# Revit family: Bath-Alcove-KOHLER-Bancroft-K-1150_1
name_source: partatom
category: Plumbing Fixtures
units: mm (PartAtom-declared; Revit-internal decimal feet)

## family parameters
Cut with Voids When Loaded = No
Host = Face
OmniClass Number = 23.31.15.00
OmniClass Title = Bathtubs
Part Type = Normal
Room Calculation Point = No
Round Connector Dimension = Use Diameter
Shared = No

## types (2) — shared parameters
ADA Compliant = No
Assembly Code = D2010500
CW Connection = No
Cold Water Inlet = Cold Water Inlet
Date Modified = 07/22/2022
Default Elevation = 0"
Drain Included = No
Finish = KOHLER-Acrylic-0-White
HW Connection = No
Height = 21 1/4"
Hot Water Inlet = Hot Water Inlet
Length = 60"
Manufacturer = Kohler Co.
Master Format 2014 = 22 41 19
Master Format 2014 Name = Residential Bathtubs
Material = Acrylic
Product Documentation Link = https://www.us.kohler.com
Product Name = Bancroft
Product Page URL = http://www.us.kohler.com
URL = https://www.us.kohler.com
Vent Connection = No
Waste Connection = Yes
Waste Water Outlet = Waste Water Outlet
WaterSense Certified = No
Width = 32"

## per-type parameters (varying)
| type | Connector Dist | Description | LA | Model | RA | Type |
| Left Hand Drain, 0-White | 9" | 60 inch x 32 inch alcove bath with integral apron, integral flange and left-hand drain | Yes | K-1150-LA-0 | No | 1 |
| Right Hand Drain, 0-White | 51" | 60 inch x 32 inch alcove bath with integral apron, integral flange and right-hand drain | No | K-1150-RA-0 | Yes | 2 |

## geometry (parser evidence)
native form markers: Sweep x5
no freeform markers — native parametric forms only
